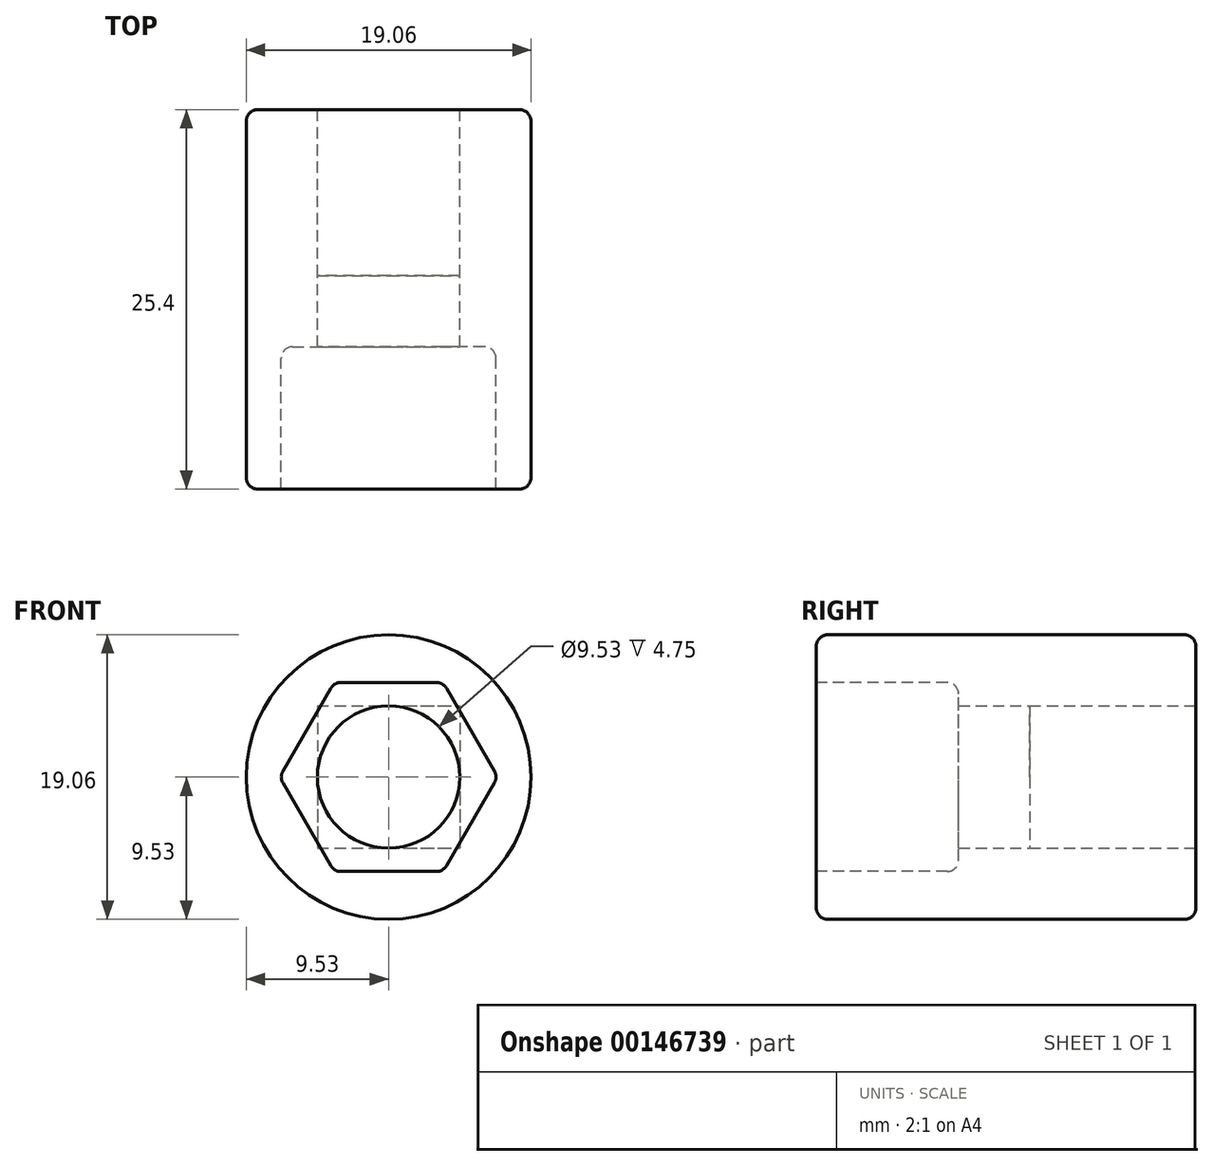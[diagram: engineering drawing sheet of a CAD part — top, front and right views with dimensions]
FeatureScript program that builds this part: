
annotation { "Feature Type Name" : "Feature", "Feature Type Description" : "" }
export const myFeature = defineFeature(function(context is Context, id is Id, definition is map)
    precondition{}
    {
        {
            var Q0;
            Q0=qCreatedBy(makeId("Front.planeOp"),FACE);
            var sketch = newSketch(context, id + "F0", { "sketchPlane" : qUnion([Q0])});
            skCircle(sketch, "E0", {"center": v(0, 0) * mm, "radius": 9.53 * mm});
            skSolve(sketch);
        }
        {
            var Q0;
            Q0 = qSketchRegion(id + "F0", true);
            extrude(context, id + "F1", {"entities" : qUnion([Q0]), "depth" : 25.4 * mm});
        }
        {
            var Q0;
            Q0=qCreatedBy(makeId("Front.planeOp"),FACE);
            var sketch = newSketch(context, id + "F2", { "sketchPlane" : qUnion([Q0])});
            skLineSegment(sketch, "E1.bottom", {"start": v(-4.76, 4.76) * mm, "end": v(4.76, 4.76) * mm});
            skLineSegment(sketch, "E1.top", {"start": v(-4.76, -4.76) * mm, "end": v(4.76, -4.76) * mm});
            skLineSegment(sketch, "E1.left", {"start": v(-4.76, 4.76) * mm, "end": v(-4.76, -4.76) * mm});
            skLineSegment(sketch, "E1.right", {"start": v(4.76, 4.76) * mm, "end": v(4.76, -4.76) * mm});
            skPoint(sketch, "E1.middle", {"position": v(0, 0) * mm});
            skCircle(sketch, "E2", {"center": v(0, 0) * mm, "radius": 4.76 * mm});
            skSolve(sketch);
        }
        {
            var Q0;
            {var subQ0=sQuery(id+"F2.wireOp",EDGE,"E2");var subQ1=makeQuery(id+"F2.imprint","INTERSECT",VERTEX,{"derivedFrom":[sQuery(id+"F2.wireOp",EDGE,"E1.bottom"),subQ0]});Q0=makeQuery(id+"F2.imprint","IMPRINT",FACE,{"disambiguationData":[TD([[makeQuery(id+"F2.imprint","IMPRINT",EDGE,{"disambiguationData":[TD([[subQ1,1.0]])],"derivedFrom":subQ0}),1.0]])]});}
            extrude(context, id + "F3", {"entities" : qUnion([Q0]), "operationType" : NewBodyOperationType.REMOVE, "endBound" : BoundingType.THROUGH_ALL, "depth" : 25.4 * mm});
        }
        {
            var Q0;
            Q0 = qSketchRegion(id + "F2", true);
            extrude(context, id + "F4", {"entities" : qUnion([Q0]), "operationType" : NewBodyOperationType.REMOVE, "depth" : 11.13 * mm});
        }
        {
            var Q0;
            Q0=makeQuery(id+"F1.opExtrude","CAP_FACE",FACE,{"disambiguationData":[OSD([sQuery(id+"F0.wireOp",EDGE,"E0")])],"isStart":false});
            var sketch = newSketch(context, id + "F5", { "sketchPlane" : qUnion([Q0])});
            skCircle(sketch, "E3.cCircle", {"center": v(0, 0) * mm, "radius": 6.32 * mm, "construction": true});
            skLineSegment(sketch, "E3.0", {"start": v(-3.65, 6.32) * mm, "end": v(3.65, 6.32) * mm});
            skLineSegment(sketch, "E3.1", {"start": v(3.65, 6.32) * mm, "end": v(7.3, 0) * mm});
            skLineSegment(sketch, "E3.2", {"start": v(7.3, 0) * mm, "end": v(3.65, -6.32) * mm});
            skLineSegment(sketch, "E3.3", {"start": v(3.65, -6.32) * mm, "end": v(-3.65, -6.32) * mm});
            skLineSegment(sketch, "E3.4", {"start": v(-3.65, -6.32) * mm, "end": v(-7.3, 0) * mm});
            skLineSegment(sketch, "E3.5", {"start": v(-7.3, 0) * mm, "end": v(-3.65, 6.32) * mm});
            skPoint(sketch, "E3.0.midPoint", {"position": v(0, 6.32) * mm});
            skSolve(sketch);
        }
        {
            var Q0;
            Q0 = qSketchRegion(id + "F5", true);
            extrude(context, id + "F6", {"entities" : qUnion([Q0]), "operationType" : NewBodyOperationType.REMOVE, "oppositeDirection" : true, "depth" : 9.52 * mm});
        }
        {
            var Q0;
            Q0=makeQuery(id+"F1.opExtrude","CAP_EDGE",EDGE,{"disambiguationData":[OSD([sQuery(id+"F0.wireOp",EDGE,"E0")])],"isStart":true});
            var Q1;
            Q1=makeQuery(id+"F1.opExtrude","CAP_EDGE",EDGE,{"disambiguationData":[OSD([sQuery(id+"F0.wireOp",EDGE,"E0")])],"isStart":false});
            fillet(context, id + "F7", {"entities" : qUnion([Q0, Q1]), "radius" : 0.76 * mm, "tangentPropagation" : true, "allowEdgeOverflow" : false});
        }
        {
            var Q0;
            Q0=makeQuery(id+"F6.boolean.opBoolean","COPY",EDGE,{"derivedFrom":makeQuery(id+"F6.opExtrude","SWEPT_EDGE",EDGE,{"disambiguationData":[OSD([sQuery(id+"F5.wireOp",EDGE,"E3.0"),sQuery(id+"F5.wireOp",EDGE,"E3.1")])]})});
            var Q1;
            Q1=makeQuery(id+"F6.boolean.opBoolean","COPY",EDGE,{"derivedFrom":makeQuery(id+"F6.opExtrude","SWEPT_EDGE",EDGE,{"disambiguationData":[OSD([sQuery(id+"F5.wireOp",EDGE,"E3.2"),sQuery(id+"F5.wireOp",EDGE,"E3.3")])]})});
            var Q2;
            Q2=makeQuery(id+"F6.boolean.opBoolean","COPY",EDGE,{"derivedFrom":makeQuery(id+"F6.opExtrude","SWEPT_EDGE",EDGE,{"disambiguationData":[OSD([sQuery(id+"F5.wireOp",EDGE,"E3.3"),sQuery(id+"F5.wireOp",EDGE,"E3.4")])]})});
            var Q3;
            Q3=makeQuery(id+"F6.boolean.opBoolean","COPY",EDGE,{"derivedFrom":makeQuery(id+"F6.opExtrude","SWEPT_EDGE",EDGE,{"disambiguationData":[OSD([sQuery(id+"F5.wireOp",EDGE,"E3.4"),sQuery(id+"F5.wireOp",EDGE,"E3.5")])]})});
            var Q4;
            Q4=makeQuery(id+"F6.boolean.opBoolean","COPY",EDGE,{"derivedFrom":makeQuery(id+"F6.opExtrude","SWEPT_EDGE",EDGE,{"disambiguationData":[OSD([sQuery(id+"F5.wireOp",EDGE,"E3.0"),sQuery(id+"F5.wireOp",EDGE,"E3.5")])]})});
            var Q5;
            Q5=makeQuery(id+"F6.boolean.opBoolean","COPY",EDGE,{"derivedFrom":makeQuery(id+"F6.opExtrude","SWEPT_EDGE",EDGE,{"disambiguationData":[OSD([sQuery(id+"F5.wireOp",EDGE,"E3.1"),sQuery(id+"F5.wireOp",EDGE,"E3.2")])]})});
            fillet(context, id + "F8", {"entities" : qUnion([Q0, Q1, Q2, Q3, Q4, Q5]), "radius" : 0.76 * mm, "tangentPropagation" : true, "defaultsChanged" : false, "vertexSettings" : [], "allowEdgeOverflow" : false});
        }
        {
            var Q0;
            Q0=makeQuery(id+"F6.boolean.opBoolean","COPY",EDGE,{"derivedFrom":makeQuery(id+"F6.opExtrude","CAP_EDGE",EDGE,{"disambiguationData":[OSD([sQuery(id+"F5.wireOp",EDGE,"E3.0")])],"isStart":false})});
            fillet(context, id + "F9", {"entities" : qUnion([Q0]), "tangentPropagation" : true, "radius" : 0.76 * mm, "defaultsChanged" : false, "vertexSettings" : [], "allowEdgeOverflow" : false});
        }
    });
